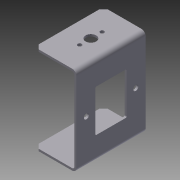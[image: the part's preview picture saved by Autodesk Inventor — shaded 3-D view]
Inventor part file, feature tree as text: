
AUTODESK INVENTOR PART (.ipt)
format: ipt  version: 2011 (Build 150239000, 239)  size: 113,152 bytes
history: native  units: mm
features: plane x2, imported_body x1
ambient origin geometry x8: Origin, YZ Plane, XZ Plane, XY Plane, X Axis, Y Axis, Z Axis, Center Point
bodies: Solid1 (feature_tree)
feature tree (3):
  imported_body  "Base1"
  plane  "Work Plane1"
  plane  "Work Plane2"
